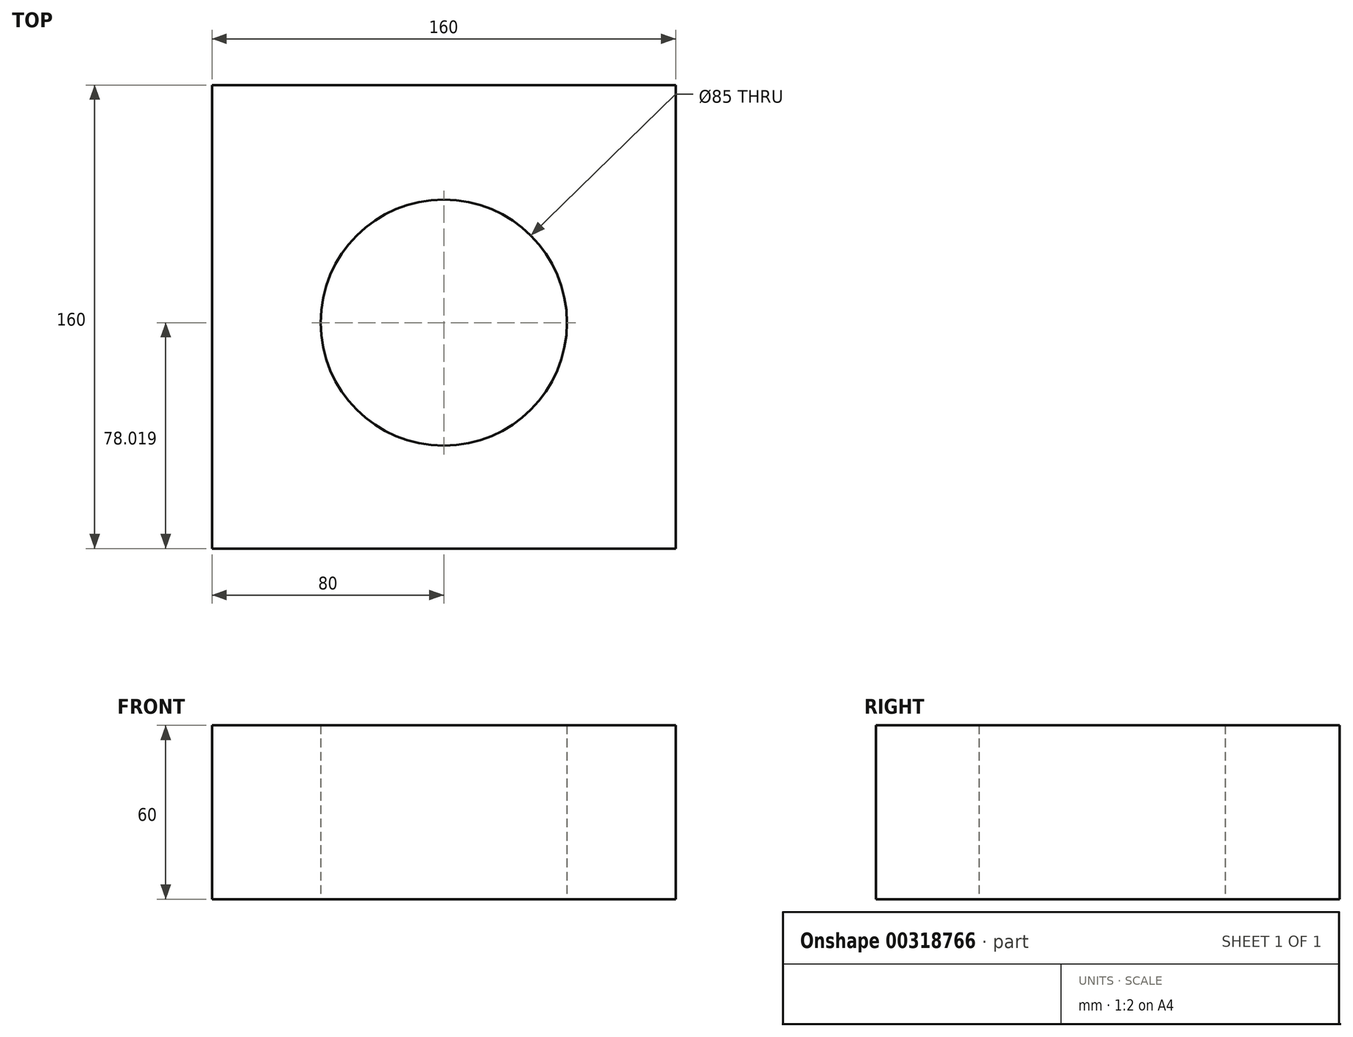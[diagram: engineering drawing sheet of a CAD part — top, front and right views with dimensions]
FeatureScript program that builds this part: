
annotation { "Feature Type Name" : "Feature", "Feature Type Description" : "" }
export const myFeature = defineFeature(function(context is Context, id is Id, definition is map)
    precondition{}
    {
        {
            var Q0;
            Q0=qCreatedBy(makeId("Top.planeOp"),FACE);
            var sketch = newSketch(context, id + "F0", { "sketchPlane" : qUnion([Q0])});
            skLineSegment(sketch, "E0.bottom", {"start": v(80, 80) * mm, "end": v(-80, 80) * mm});
            skLineSegment(sketch, "E0.top", {"start": v(80, -80) * mm, "end": v(-80, -80) * mm});
            skLineSegment(sketch, "E0.left", {"start": v(80, 80) * mm, "end": v(80, -80) * mm});
            skLineSegment(sketch, "E0.right", {"start": v(-80, 80) * mm, "end": v(-80, -80) * mm});
            skPoint(sketch, "E0.middle", {"position": v(0, 0) * mm});
            skCircle(sketch, "E1", {"center": v(0, -1.98) * mm, "radius": 42.5 * mm});
            skSolve(sketch);
        }
        {
            var Q0;
            Q0=makeQuery(id+"F0.imprint","IMPRINT",FACE,{"disambiguationData":[TD([[makeQuery(id+"F0.imprint","IMPRINT",EDGE,{"derivedFrom":sQuery(id+"F0.wireOp",EDGE,"E0.bottom")}),1.0]])]});
            extrude(context, id + "F1", {"entities" : qUnion([Q0]), "depth" : 60 * mm, "offsetDistance" : 25 * mm});
        }
    });
